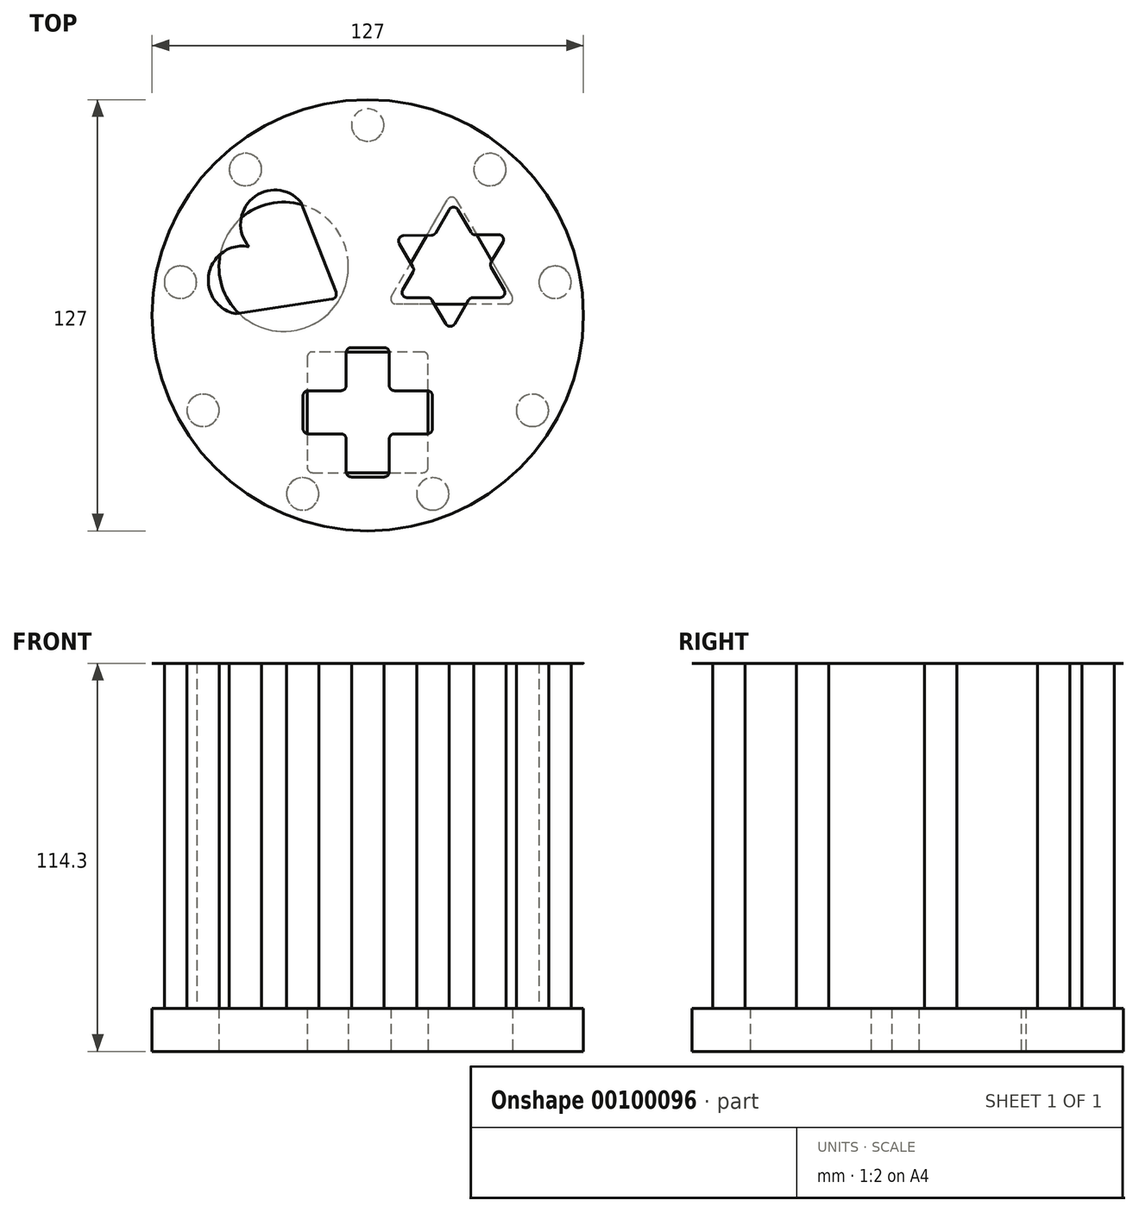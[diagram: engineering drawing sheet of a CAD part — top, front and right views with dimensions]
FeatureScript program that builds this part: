
annotation { "Feature Type Name" : "Feature", "Feature Type Description" : "" }
export const myFeature = defineFeature(function(context is Context, id is Id, definition is map)
    precondition{}
    {
        {
            var Q0;
            Q0=qCreatedBy(makeId("Top.planeOp"),FACE);
            var sketch = newSketch(context, id + "F0", { "sketchPlane" : qUnion([Q0])});
            skCircle(sketch, "E0", {"center": v(0, 0) * mm, "radius": 63.5 * mm});
            skLineSegment(sketch, "E1", {"start": v(7, 5.54) * mm, "end": v(23.45, 34.03) * mm});
            skLineSegment(sketch, "E2", {"start": v(26.05, 34.03) * mm, "end": v(42.5, 5.54) * mm});
            skLineSegment(sketch, "E3", {"start": v(41.2, 3.29) * mm, "end": v(8.3, 3.29) * mm});
            skLineSegment(sketch, "E4", {"start": v(-17.78, -12.3) * mm, "end": v(-17.78, -44.86) * mm});
            skLineSegment(sketch, "E5", {"start": v(-16.28, -46.36) * mm, "end": v(16.28, -46.36) * mm});
            skLineSegment(sketch, "E6", {"start": v(17.78, -44.86) * mm, "end": v(17.78, -12.3) * mm});
            skLineSegment(sketch, "E7", {"start": v(16.28, -10.8) * mm, "end": v(-16.28, -10.8) * mm});
            skCircle(sketch, "E8", {"center": v(-24.75, 14.29) * mm, "radius": 19.05 * mm});
            skLineSegment(sketch, "E9", {"start": v(0, 0) * mm, "end": v(78.78, 45.48) * mm, "construction": true});
            skLineSegment(sketch, "E10", {"start": v(0, 0) * mm, "end": v(-66.6, 38.45) * mm, "construction": true});
            skLineSegment(sketch, "E11", {"start": v(15.22, 19.79) * mm, "end": v(43.8, 3.29) * mm, "construction": true});
            skLineSegment(sketch, "E12", {"start": v(24.75, 36.28) * mm, "end": v(24.75, 3.29) * mm, "construction": true});
            skLineSegment(sketch, "E13", {"start": v(-17.78, -28.58) * mm, "end": v(17.78, -28.57) * mm, "construction": true});
            skCircle(sketch, "E14", {"center": v(0, 0) * mm, "radius": 28.58 * mm, "construction": true});
            skPoint(sketch, "E15", {"position": v(0, -28.58) * mm});
            skPoint(sketch, "E16", {"position": v(24.75, 14.29) * mm});
            skPoint(sketch, "E17.visualSharp", {"position": v(17.78, -46.36) * mm});
            skArc(sketch, "E17.filletArc", {"start": v(16.28, -46.36) * mm, "mid": v(17.34, -45.92) * mm, "end": v(17.78, -44.86) * mm});
            skPoint(sketch, "E18.visualSharp", {"position": v(17.78, -10.8) * mm});
            skArc(sketch, "E18.filletArc", {"start": v(17.78, -12.3) * mm, "mid": v(17.34, -11.23) * mm, "end": v(16.28, -10.8) * mm});
            skPoint(sketch, "E19.visualSharp", {"position": v(-17.78, -10.8) * mm});
            skArc(sketch, "E19.filletArc", {"start": v(-16.28, -10.8) * mm, "mid": v(-17.34, -11.23) * mm, "end": v(-17.78, -12.3) * mm});
            skPoint(sketch, "E20.visualSharp", {"position": v(-17.78, -46.36) * mm});
            skArc(sketch, "E20.filletArc", {"start": v(-17.78, -44.86) * mm, "mid": v(-17.34, -45.92) * mm, "end": v(-16.28, -46.36) * mm});
            skPoint(sketch, "E21.visualSharp", {"position": v(5.7, 3.29) * mm});
            skArc(sketch, "E21.filletArc", {"start": v(7, 5.54) * mm, "mid": v(7, 4.04) * mm, "end": v(8.3, 3.29) * mm});
            skPoint(sketch, "E22.visualSharp", {"position": v(24.75, 36.28) * mm});
            skArc(sketch, "E22.filletArc", {"start": v(26.05, 34.03) * mm, "mid": v(24.75, 34.78) * mm, "end": v(23.45, 34.03) * mm});
            skPoint(sketch, "E23.visualSharp", {"position": v(43.8, 3.29) * mm});
            skArc(sketch, "E23.filletArc", {"start": v(41.2, 3.29) * mm, "mid": v(42.5, 4.04) * mm, "end": v(42.5, 5.54) * mm});
            skSolve(sketch);
        }
        {
            var Q0;
            Q0 = qSketchRegion(id + "F0", true);
            extrude(context, id + "F1", {"entities" : qUnion([Q0]), "depth" : 12.7 * mm});
        }
        {
            var Q0;
            Q0=makeQuery(id+"F1.opExtrude","CAP_FACE",FACE,{"disambiguationData":[OSD([sQuery(id+"F0.wireOp",EDGE,"E0"),sQuery(id+"F0.wireOp",EDGE,"E1"),sQuery(id+"F0.wireOp",EDGE,"E2"),sQuery(id+"F0.wireOp",EDGE,"E3"),sQuery(id+"F0.wireOp",EDGE,"E4"),sQuery(id+"F0.wireOp",EDGE,"E5"),sQuery(id+"F0.wireOp",EDGE,"E6"),sQuery(id+"F0.wireOp",EDGE,"E7"),sQuery(id+"F0.wireOp",EDGE,"E8")])],"isStart":false});
            var sketch = newSketch(context, id + "F2", { "sketchPlane" : qUnion([Q0])});
            skCircle(sketch, "E24", {"center": v(0, 56) * mm, "radius": 4.76 * mm});
            skCircle(sketch, "E25.1.0", {"center": v(-36, 42.9) * mm, "radius": 4.76 * mm});
            skCircle(sketch, "E25.2.0", {"center": v(-55.15, 9.72) * mm, "radius": 4.76 * mm});
            skCircle(sketch, "E25.3.0", {"center": v(-48.5, -28) * mm, "radius": 4.76 * mm});
            skCircle(sketch, "E25.4.0", {"center": v(-19.15, -52.62) * mm, "radius": 4.76 * mm});
            skCircle(sketch, "E25.5.0", {"center": v(19.15, -52.62) * mm, "radius": 4.76 * mm});
            skCircle(sketch, "E25.6.0", {"center": v(48.5, -28) * mm, "radius": 4.76 * mm});
            skCircle(sketch, "E25.7.0", {"center": v(55.15, 9.72) * mm, "radius": 4.76 * mm});
            skCircle(sketch, "E25.8.0", {"center": v(36, 42.9) * mm, "radius": 4.76 * mm});
            skPoint(sketch, "E25.center", {"position": v(0, 0) * mm});
            skSolve(sketch);
        }
        {
            var Q0;
            Q0 = qSketchRegion(id + "F2", true);
            extrude(context, id + "F3", {"entities" : qUnion([Q0]), "operationType" : NewBodyOperationType.REMOVE, "oppositeDirection" : true, "depth" : 1 / 101.6 * mm});
        }
        {
            var Q0;
            Q0=makeQuery(id+"F3.boolean.opBoolean","COPY",FACE,{"derivedFrom":makeQuery(id+"F3.opExtrude","CAP_FACE",FACE,{"disambiguationData":[OSD([sQuery(id+"F2.wireOp",EDGE,"E24")])],"isStart":false})});
            var sketch = newSketch(context, id + "F4", { "sketchPlane" : qUnion([Q0])});
            skCircle(sketch, "E26.0", {"center": v(0, 56) * mm, "radius": 4.76 * mm});
            skSolve(sketch);
        }
        {
            var Q0;
            Q0 = qSketchRegion(id + "F4", true);
            extrude(context, id + "F5", {"entities" : qUnion([Q0]), "depth" : 101.6 * mm});
        }
        {
            var Q0;
            Q0=qCreatedBy(makeId("Front.planeOp"),FACE);
            var sketch = newSketch(context, id + "F6", { "sketchPlane" : qUnion([Q0])});
            skLineSegment(sketch, "E27", {"start": v(0, 0) * mm, "end": v(0, 70.86) * mm, "construction": true});
            skSolve(sketch);
        }
        {
            var Q0;
            Q0=makeQuery(id+"F5.opExtrude","SWEPT_BODY",BODY,{"disambiguationData":[OSD([sQuery(id+"F4.wireOp",EDGE,"E26.0")])]});
            var Q1;
            Q1=sQuery(id+"F6.wireOp",EDGE,"E27");
            circularPattern(context, id + "F7", {"entities" : qUnion([Q0]), "axis" : qUnion([Q1]), "angle" : 40 * degree, "instanceCount" : 9});
        }
        {
            var Q0;
            Q0=makeQuery(id+"F5.opExtrude","CAP_FACE",FACE,{"disambiguationData":[OSD([sQuery(id+"F4.wireOp",EDGE,"E26.0")])],"isStart":false});
            cPlane(context, id + "F8", {"entities" : qUnion([Q0]), "cplaneType" : CPlaneType.OFFSET, "offset" : 1 / 101.6 * mm, "oppositeDirection" : true, "width" : 150 * mm, "height" : 150 * mm});
        }
        {
            var Q0;
            Q0=qCreatedBy(id+"F8.planeOp",FACE);
            var sketch = newSketch(context, id + "F9", { "sketchPlane" : qUnion([Q0])});
            skCircle(sketch, "E28.0", {"center": v(0, 0) * mm, "radius": 63.5 * mm});
            skLineSegment(sketch, "E29", {"start": v(0, 0) * mm, "end": v(-103.86, 59.96) * mm, "construction": true});
            skLineSegment(sketch, "E30", {"start": v(-4.85, -9.53) * mm, "end": v(4.85, -9.53) * mm});
            skLineSegment(sketch, "E31", {"start": v(6.35, -11.03) * mm, "end": v(6.35, -20.73) * mm});
            skLineSegment(sketch, "E32", {"start": v(7.85, -22.23) * mm, "end": v(17.55, -22.23) * mm});
            skLineSegment(sketch, "E33", {"start": v(19.05, -23.73) * mm, "end": v(19.05, -33.42) * mm});
            skLineSegment(sketch, "E34", {"start": v(17.55, -34.92) * mm, "end": v(7.85, -34.92) * mm});
            skLineSegment(sketch, "E35", {"start": v(6.35, -36.43) * mm, "end": v(6.35, -46.13) * mm});
            skLineSegment(sketch, "E36", {"start": v(4.85, -47.63) * mm, "end": v(-4.85, -47.63) * mm});
            skLineSegment(sketch, "E37", {"start": v(-6.35, -46.13) * mm, "end": v(-6.35, -36.42) * mm});
            skLineSegment(sketch, "E38", {"start": v(-7.85, -34.92) * mm, "end": v(-17.55, -34.92) * mm});
            skLineSegment(sketch, "E39", {"start": v(-19.05, -33.43) * mm, "end": v(-19.05, -23.73) * mm});
            skLineSegment(sketch, "E40", {"start": v(-17.55, -22.23) * mm, "end": v(-7.85, -22.23) * mm});
            skLineSegment(sketch, "E41", {"start": v(-6.35, -20.73) * mm, "end": v(-6.35, -11.03) * mm});
            skLineSegment(sketch, "E42", {"start": v(-10.51, 4.72) * mm, "end": v(-38.8, 0.4) * mm});
            skLineSegment(sketch, "E43", {"start": v(-19.74, 33.4) * mm, "end": v(-9.34, 6.75) * mm});
            skArc(sketch, "E44", {"start": v(-34.97, 20.19) * mm, "mid": v(-46.78, 12.2) * mm, "end": v(-38.8, 0.4) * mm});
            skArc(sketch, "E45", {"start": v(-19.74, 33.4) * mm, "mid": v(-33.96, 34.4) * mm, "end": v(-34.97, 20.19) * mm});
            skPoint(sketch, "E46.start.orphan", {"position": v(-29.27, 16.9) * mm});
            skLineSegment(sketch, "E47", {"start": v(0, 0) * mm, "end": v(63.74, 36.8) * mm, "construction": true});
            skLineSegment(sketch, "E48", {"start": v(23.94, 31.08) * mm, "end": v(20, 24.25) * mm});
            skLineSegment(sketch, "E49", {"start": v(11.6, 5.2) * mm, "end": v(17.64, 5.2) * mm});
            skLineSegment(sketch, "E50", {"start": v(40.19, 7.45) * mm, "end": v(36.33, 14.12) * mm});
            skLineSegment(sketch, "E51", {"start": v(38.5, 23.73) * mm, "end": v(31.71, 23.65) * mm});
            skLineSegment(sketch, "E52", {"start": v(9.29, 21.16) * mm, "end": v(13.32, 14.18) * mm});
            skLineSegment(sketch, "E53", {"start": v(25.56, -2.55) * mm, "end": v(29.72, 4.46) * mm});
            skLineSegment(sketch, "E54.trimOffspring", {"start": v(13.32, 12.68) * mm, "end": v(10.3, 7.45) * mm});
            skLineSegment(sketch, "E55.trimOffspring", {"start": v(18.72, 23.5) * mm, "end": v(10.57, 23.4) * mm});
            skLineSegment(sketch, "E56.trimOffspring", {"start": v(30.4, 24.4) * mm, "end": v(26.54, 31.08) * mm});
            skLineSegment(sketch, "E57.trimOffspring", {"start": v(36.34, 15.64) * mm, "end": v(39.8, 21.47) * mm});
            skLineSegment(sketch, "E58.trimOffspring", {"start": v(31, 5.2) * mm, "end": v(38.89, 5.2) * mm});
            skLineSegment(sketch, "E59.trimOffspring", {"start": v(18.94, 4.45) * mm, "end": v(22.97, -2.54) * mm});
            skLineSegment(sketch, "E60", {"start": v(19.05, -28.58) * mm, "end": v(-19.05, -28.58) * mm, "construction": true});
            skLineSegment(sketch, "E61", {"start": v(0, -47.63) * mm, "end": v(0, -9.52) * mm, "construction": true});
            skLineSegment(sketch, "E62", {"start": v(41.49, 5.2) * mm, "end": v(8, 23.38) * mm, "construction": true});
            skLineSegment(sketch, "E63", {"start": v(24.25, -4.76) * mm, "end": v(25.24, 33.33) * mm, "construction": true});
            skPoint(sketch, "E64", {"position": v(24.75, 14.29) * mm});
            skPoint(sketch, "E65", {"position": v(0, -28.58) * mm});
            skPoint(sketch, "E66.visualSharp", {"position": v(41.16, 23.76) * mm});
            skArc(sketch, "E66.filletArc", {"start": v(39.8, 21.47) * mm, "mid": v(39.8, 22.98) * mm, "end": v(38.5, 23.73) * mm});
            skPoint(sketch, "E67.visualSharp", {"position": v(41.49, 5.2) * mm});
            skArc(sketch, "E67.filletArc", {"start": v(38.89, 5.2) * mm, "mid": v(40.19, 5.95) * mm, "end": v(40.19, 7.45) * mm});
            skPoint(sketch, "E68.visualSharp", {"position": v(24.25, -4.76) * mm});
            skArc(sketch, "E68.filletArc", {"start": v(22.97, -2.54) * mm, "mid": v(24.26, -3.29) * mm, "end": v(25.56, -2.55) * mm});
            skPoint(sketch, "E69.visualSharp", {"position": v(9, 5.2) * mm});
            skArc(sketch, "E69.filletArc", {"start": v(10.3, 7.45) * mm, "mid": v(10.3, 5.95) * mm, "end": v(11.6, 5.2) * mm});
            skPoint(sketch, "E70.visualSharp", {"position": v(8, 23.38) * mm});
            skArc(sketch, "E70.filletArc", {"start": v(10.57, 23.4) * mm, "mid": v(9.28, 22.65) * mm, "end": v(9.29, 21.16) * mm});
            skPoint(sketch, "E71.visualSharp", {"position": v(25.24, 33.33) * mm});
            skArc(sketch, "E71.filletArc", {"start": v(26.54, 31.08) * mm, "mid": v(25.24, 31.83) * mm, "end": v(23.94, 31.08) * mm});
            skPoint(sketch, "E72.visualSharp", {"position": v(19.58, 23.51) * mm});
            skArc(sketch, "E72.filletArc", {"start": v(18.72, 23.5) * mm, "mid": v(19.46, 23.7) * mm, "end": v(20, 24.25) * mm});
            skPoint(sketch, "E73.visualSharp", {"position": v(13.75, 13.43) * mm});
            skArc(sketch, "E73.filletArc", {"start": v(13.32, 12.68) * mm, "mid": v(13.52, 13.43) * mm, "end": v(13.32, 14.18) * mm});
            skPoint(sketch, "E74.visualSharp", {"position": v(18.5, 5.2) * mm});
            skArc(sketch, "E74.filletArc", {"start": v(18.94, 4.45) * mm, "mid": v(18.39, 5) * mm, "end": v(17.64, 5.2) * mm});
            skPoint(sketch, "E75.visualSharp", {"position": v(30.15, 5.2) * mm});
            skArc(sketch, "E75.filletArc", {"start": v(31, 5.2) * mm, "mid": v(30.26, 5) * mm, "end": v(29.72, 4.46) * mm});
            skPoint(sketch, "E76.visualSharp", {"position": v(35.9, 14.88) * mm});
            skArc(sketch, "E76.filletArc", {"start": v(36.34, 15.64) * mm, "mid": v(36.13, 14.88) * mm, "end": v(36.33, 14.12) * mm});
            skPoint(sketch, "E77.visualSharp", {"position": v(30.84, 23.64) * mm});
            skArc(sketch, "E77.filletArc", {"start": v(30.4, 24.4) * mm, "mid": v(30.95, 23.85) * mm, "end": v(31.71, 23.65) * mm});
            skPoint(sketch, "E78.visualSharp", {"position": v(6.35, -22.23) * mm});
            skArc(sketch, "E78.filletArc", {"start": v(6.35, -20.73) * mm, "mid": v(6.79, -21.79) * mm, "end": v(7.85, -22.23) * mm});
            skPoint(sketch, "E79.visualSharp", {"position": v(6.35, -34.92) * mm});
            skArc(sketch, "E79.filletArc", {"start": v(7.85, -34.93) * mm, "mid": v(6.79, -35.36) * mm, "end": v(6.35, -36.43) * mm});
            skPoint(sketch, "E80.visualSharp", {"position": v(-6.35, -34.93) * mm});
            skArc(sketch, "E80.filletArc", {"start": v(-6.35, -36.42) * mm, "mid": v(-6.79, -35.36) * mm, "end": v(-7.85, -34.92) * mm});
            skPoint(sketch, "E81.visualSharp", {"position": v(-6.35, -22.23) * mm});
            skArc(sketch, "E81.filletArc", {"start": v(-7.85, -22.23) * mm, "mid": v(-6.79, -21.79) * mm, "end": v(-6.35, -20.73) * mm});
            skPoint(sketch, "E82.visualSharp", {"position": v(-19.05, -22.23) * mm});
            skArc(sketch, "E82.filletArc", {"start": v(-17.55, -22.23) * mm, "mid": v(-18.61, -22.66) * mm, "end": v(-19.05, -23.73) * mm});
            skPoint(sketch, "E83.visualSharp", {"position": v(-19.05, -34.92) * mm});
            skArc(sketch, "E83.filletArc", {"start": v(-19.05, -33.43) * mm, "mid": v(-18.61, -34.49) * mm, "end": v(-17.55, -34.93) * mm});
            skPoint(sketch, "E84.visualSharp", {"position": v(-6.35, -47.63) * mm});
            skArc(sketch, "E84.filletArc", {"start": v(-6.35, -46.13) * mm, "mid": v(-5.91, -47.19) * mm, "end": v(-4.85, -47.62) * mm});
            skPoint(sketch, "E85.visualSharp", {"position": v(6.35, -47.63) * mm});
            skArc(sketch, "E85.filletArc", {"start": v(4.85, -47.63) * mm, "mid": v(5.91, -47.19) * mm, "end": v(6.35, -46.13) * mm});
            skPoint(sketch, "E86.visualSharp", {"position": v(19.05, -34.93) * mm});
            skArc(sketch, "E86.filletArc", {"start": v(17.55, -34.92) * mm, "mid": v(18.61, -34.49) * mm, "end": v(19.05, -33.42) * mm});
            skPoint(sketch, "E87.visualSharp", {"position": v(19.05, -22.23) * mm});
            skArc(sketch, "E87.filletArc", {"start": v(19.05, -23.73) * mm, "mid": v(18.61, -22.66) * mm, "end": v(17.55, -22.23) * mm});
            skPoint(sketch, "E88.visualSharp", {"position": v(6.35, -9.53) * mm});
            skArc(sketch, "E88.filletArc", {"start": v(6.35, -11.03) * mm, "mid": v(5.91, -9.96) * mm, "end": v(4.85, -9.53) * mm});
            skPoint(sketch, "E89.visualSharp", {"position": v(-6.35, -9.53) * mm});
            skArc(sketch, "E89.filletArc", {"start": v(-4.85, -9.53) * mm, "mid": v(-5.91, -9.96) * mm, "end": v(-6.35, -11.03) * mm});
            skPoint(sketch, "E90.visualSharp", {"position": v(-8.66, 5) * mm});
            skArc(sketch, "E90.filletArc", {"start": v(-10.51, 4.72) * mm, "mid": v(-9.44, 5.45) * mm, "end": v(-9.34, 6.75) * mm});
            skSolve(sketch);
        }
        {
            var Q0;
            Q0 = qSketchRegion(id + "F9", true);
            extrude(context, id + "F10", {"entities" : qUnion([Q0]), "depth" : 1 / 50.8 * mm});
        }
        {
            var Q0;
            Q0=makeQuery(id+"F10.opExtrude","CAP_FACE",FACE,{"disambiguationData":[OSD([sQuery(id+"F9.wireOp",EDGE,"E28.0"),sQuery(id+"F9.wireOp",EDGE,"E30"),sQuery(id+"F9.wireOp",EDGE,"E31"),sQuery(id+"F9.wireOp",EDGE,"E32"),sQuery(id+"F9.wireOp",EDGE,"E33"),sQuery(id+"F9.wireOp",EDGE,"E34"),sQuery(id+"F9.wireOp",EDGE,"E35"),sQuery(id+"F9.wireOp",EDGE,"E36"),sQuery(id+"F9.wireOp",EDGE,"E37"),sQuery(id+"F9.wireOp",EDGE,"E38"),sQuery(id+"F9.wireOp",EDGE,"E39"),sQuery(id+"F9.wireOp",EDGE,"E40"),sQuery(id+"F9.wireOp",EDGE,"E41"),sQuery(id+"F9.wireOp",EDGE,"E42"),sQuery(id+"F9.wireOp",EDGE,"E43"),sQuery(id+"F9.wireOp",EDGE,"E44"),sQuery(id+"F9.wireOp",EDGE,"E45"),sQuery(id+"F9.wireOp",EDGE,"E48"),sQuery(id+"F9.wireOp",EDGE,"E49"),sQuery(id+"F9.wireOp",EDGE,"E50"),sQuery(id+"F9.wireOp",EDGE,"E51"),sQuery(id+"F9.wireOp",EDGE,"E52"),sQuery(id+"F9.wireOp",EDGE,"E53"),sQuery(id+"F9.wireOp",EDGE,"E54.trimOffspring"),sQuery(id+"F9.wireOp",EDGE,"E55.trimOffspring"),sQuery(id+"F9.wireOp",EDGE,"E56.trimOffspring"),sQuery(id+"F9.wireOp",EDGE,"E57.trimOffspring"),sQuery(id+"F9.wireOp",EDGE,"E58.trimOffspring"),sQuery(id+"F9.wireOp",EDGE,"E59.trimOffspring")])],"isStart":true});
            var sketch = newSketch(context, id + "F11", { "sketchPlane" : qUnion([Q0])});
            skCircle(sketch, "E91.0", {"center": v(-19.15, 52.62) * mm, "radius": 4.76 * mm});
            skCircle(sketch, "E92.1.0", {"center": v(-48.5, 28) * mm, "radius": 4.76 * mm});
            skCircle(sketch, "E92.2.0", {"center": v(-55.15, -9.72) * mm, "radius": 4.76 * mm});
            skCircle(sketch, "E92.3.0", {"center": v(-36, -42.9) * mm, "radius": 4.76 * mm});
            skCircle(sketch, "E92.4.0", {"center": v(0, -56) * mm, "radius": 4.76 * mm});
            skCircle(sketch, "E92.5.0", {"center": v(36, -42.9) * mm, "radius": 4.76 * mm});
            skCircle(sketch, "E92.6.0", {"center": v(55.15, -9.72) * mm, "radius": 4.76 * mm});
            skCircle(sketch, "E92.7.0", {"center": v(48.5, 28) * mm, "radius": 4.76 * mm});
            skCircle(sketch, "E92.8.0", {"center": v(19.15, 52.62) * mm, "radius": 4.76 * mm});
            skPoint(sketch, "E92.center", {"position": v(0, 0) * mm});
            skSolve(sketch);
        }
        {
            var Q0;
            Q0 = qSketchRegion(id + "F11", true);
            extrude(context, id + "F12", {"entities" : qUnion([Q0]), "operationType" : NewBodyOperationType.REMOVE, "oppositeDirection" : true, "depth" : 1 / 101.6 * mm});
        }
    });
